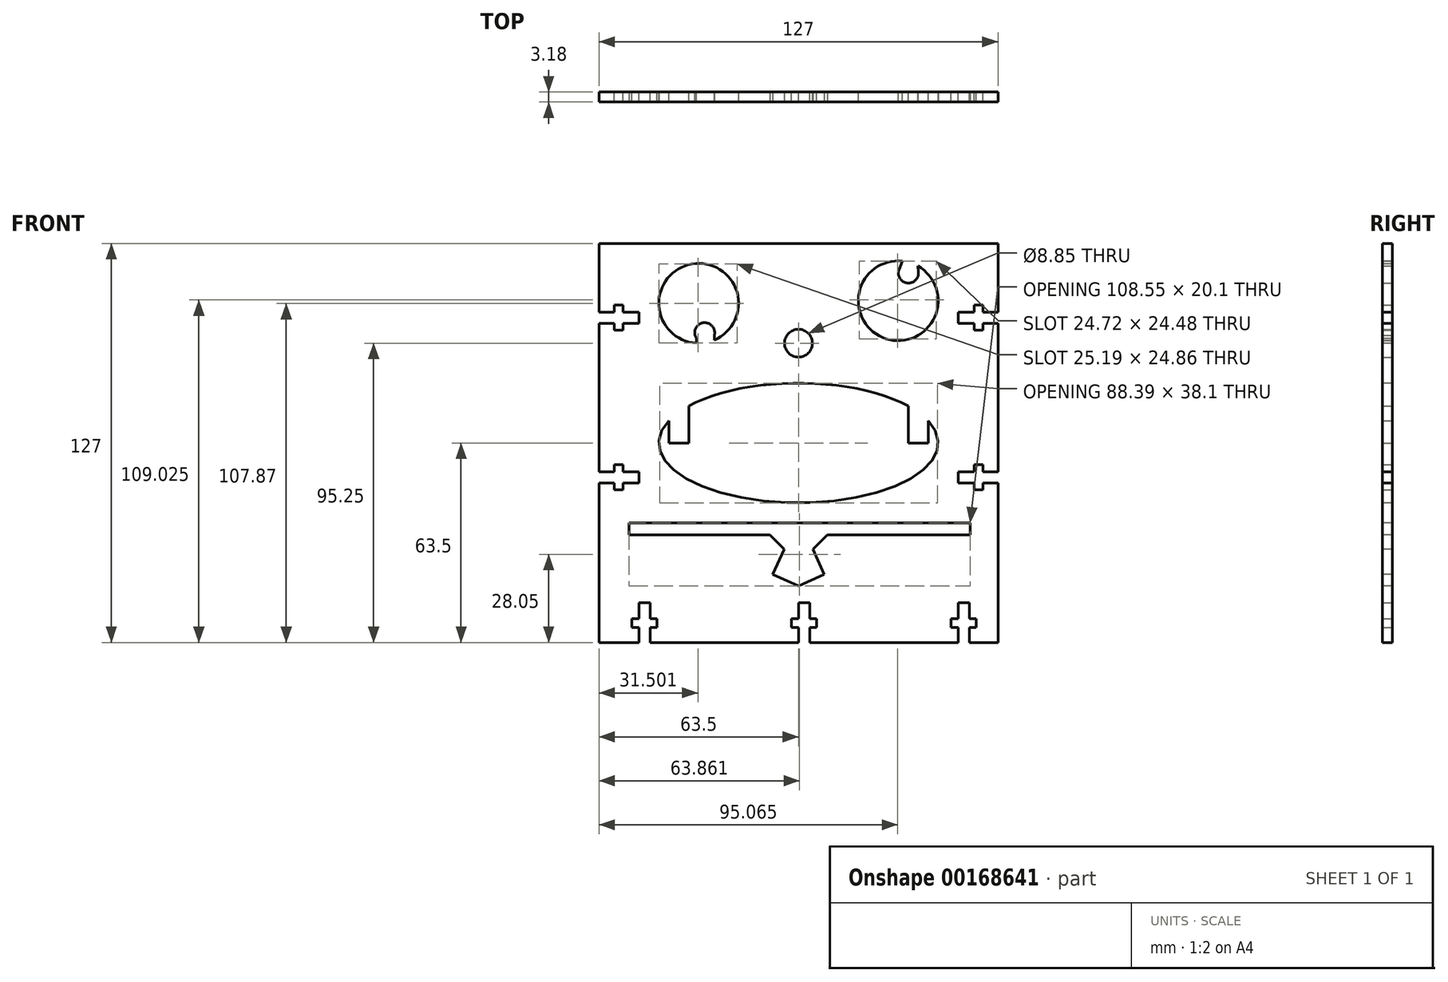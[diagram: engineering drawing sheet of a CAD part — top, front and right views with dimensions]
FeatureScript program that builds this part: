
annotation { "Feature Type Name" : "Feature", "Feature Type Description" : "" }
export const myFeature = defineFeature(function(context is Context, id is Id, definition is map)
    precondition{}
    {
        {
            var Q0;
            Q0=qCreatedBy(makeId("Front.planeOp"),FACE);
            var sketch = newSketch(context, id + "F0", { "sketchPlane" : qUnion([Q0])});
            skLineSegment(sketch, "E0.bottom", {"start": v(63.5, -63.5) * mm, "end": v(-63.5, -63.5) * mm});
            skLineSegment(sketch, "E0.top", {"start": v(63.5, 63.5) * mm, "end": v(-63.5, 63.5) * mm});
            skLineSegment(sketch, "E0.left", {"start": v(63.5, -63.5) * mm, "end": v(63.5, 63.5) * mm});
            skLineSegment(sketch, "E0.right", {"start": v(-63.5, -63.5) * mm, "end": v(-63.5, 63.5) * mm});
            skPoint(sketch, "E0.middle", {"position": v(0, 0) * mm});
            skEllipse(sketch, "E1", {"center": v(0, 0) * mm, "majorRadius": 44.45 * mm, "minorRadius": 19.05 * mm, "majorAxis": v(1, 0)});
            skLineSegment(sketch, "E2", {"start": v(-34.93, 11.78) * mm, "end": v(-34.93, 0) * mm});
            skLineSegment(sketch, "E3", {"start": v(-41.28, 0) * mm, "end": v(-34.93, 0) * mm});
            skLineSegment(sketch, "E4", {"start": v(-41.28, 0) * mm, "end": v(-41.28, 7.07) * mm});
            skLineSegment(sketch, "E5", {"start": v(41.28, 7.07) * mm, "end": v(41.28, 0) * mm});
            skLineSegment(sketch, "E6", {"start": v(34.93, 0) * mm, "end": v(41.28, 0) * mm});
            skLineSegment(sketch, "E7", {"start": v(34.93, 0) * mm, "end": v(34.93, 11.78) * mm});
            skCircle(sketch, "E8", {"center": v(0, 31.75) * mm, "radius": 4.43 * mm});
            skCircle(sketch, "E9", {"center": v(-31.75, 44.45) * mm, "radius": 12.7 * mm});
            skArc(sketch, "E10", {"start": v(-26.78, 34.27) * mm, "mid": v(-30.31, 38.26) * mm, "end": v(-32.52, 33.41) * mm});
            skCircle(sketch, "E11", {"center": v(31.75, 45.26) * mm, "radius": 12.7 * mm});
            skArc(sketch, "E12", {"start": v(32.04, 55.22) * mm, "mid": v(34.52, 50.92) * mm, "end": v(38.17, 54.28) * mm});
            skLineSegment(sketch, "E13", {"start": v(32.04, 55.22) * mm, "end": v(33.09, 57.88) * mm});
            skLineSegment(sketch, "E14", {"start": v(38.17, 54.28) * mm, "end": v(38.03, 56.3) * mm});
            skLineSegment(sketch, "E15", {"start": v(-32.52, 33.41) * mm, "end": v(-32.52, 31.77) * mm});
            skLineSegment(sketch, "E16", {"start": v(-26.78, 34.27) * mm, "end": v(-26.78, 32.76) * mm});
            skLineSegment(sketch, "E17", {"start": v(-50.8, -58.66) * mm, "end": v(-50.8, -63.5) * mm});
            skLineSegment(sketch, "E18", {"start": v(-50.8, -58.66) * mm, "end": v(-53, -58.66) * mm});
            skLineSegment(sketch, "E19", {"start": v(-53, -58.66) * mm, "end": v(-53, -55.88) * mm});
            skLineSegment(sketch, "E20", {"start": v(-53, -55.88) * mm, "end": v(-50.8, -55.88) * mm});
            skLineSegment(sketch, "E21", {"start": v(-50.8, -55.88) * mm, "end": v(-50.8, -50.8) * mm});
            skLineSegment(sketch, "E22", {"start": v(-50.8, -50.8) * mm, "end": v(-47.24, -50.8) * mm});
            skLineSegment(sketch, "E23", {"start": v(-47.24, -50.8) * mm, "end": v(-47.24, -55.88) * mm});
            skLineSegment(sketch, "E24", {"start": v(-47.24, -55.88) * mm, "end": v(-45.05, -55.88) * mm});
            skLineSegment(sketch, "E25", {"start": v(-45.05, -55.88) * mm, "end": v(-45.05, -58.66) * mm});
            skLineSegment(sketch, "E26", {"start": v(-45.05, -58.66) * mm, "end": v(-47.24, -58.66) * mm});
            skLineSegment(sketch, "E27", {"start": v(-47.24, -58.66) * mm, "end": v(-47.24, -63.5) * mm});
            skLineSegment(sketch, "E28.1.0.0", {"start": v(0, -58.66) * mm, "end": v(0, -63.5) * mm});
            skLineSegment(sketch, "E28.1.0.1", {"start": v(3.56, -58.66) * mm, "end": v(3.56, -63.5) * mm});
            skLineSegment(sketch, "E28.1.0.2", {"start": v(3.56, -50.8) * mm, "end": v(3.56, -55.88) * mm});
            skLineSegment(sketch, "E28.1.0.3", {"start": v(-2.2, -55.88) * mm, "end": v(0, -55.88) * mm});
            skLineSegment(sketch, "E28.1.0.4", {"start": v(0, -55.88) * mm, "end": v(0, -50.8) * mm});
            skLineSegment(sketch, "E28.1.0.5", {"start": v(0, -58.66) * mm, "end": v(-2.2, -58.66) * mm});
            skLineSegment(sketch, "E28.1.0.6", {"start": v(0, -50.8) * mm, "end": v(3.56, -50.8) * mm});
            skLineSegment(sketch, "E28.1.0.7", {"start": v(-2.2, -58.66) * mm, "end": v(-2.2, -55.88) * mm});
            skLineSegment(sketch, "E28.1.0.8", {"start": v(3.56, -55.88) * mm, "end": v(5.75, -55.88) * mm});
            skLineSegment(sketch, "E28.1.0.9", {"start": v(5.75, -55.88) * mm, "end": v(5.75, -58.66) * mm});
            skLineSegment(sketch, "E28.1.0.10", {"start": v(5.75, -58.66) * mm, "end": v(3.56, -58.66) * mm});
            skLineSegment(sketch, "E28.2.0.0", {"start": v(50.8, -58.66) * mm, "end": v(50.8, -63.5) * mm});
            skLineSegment(sketch, "E28.2.0.1", {"start": v(54.36, -58.66) * mm, "end": v(54.36, -63.5) * mm});
            skLineSegment(sketch, "E28.2.0.2", {"start": v(54.36, -50.8) * mm, "end": v(54.36, -55.88) * mm});
            skLineSegment(sketch, "E28.2.0.3", {"start": v(48.6, -55.88) * mm, "end": v(50.8, -55.88) * mm});
            skLineSegment(sketch, "E28.2.0.4", {"start": v(50.8, -55.88) * mm, "end": v(50.8, -50.8) * mm});
            skLineSegment(sketch, "E28.2.0.5", {"start": v(50.8, -58.66) * mm, "end": v(48.6, -58.66) * mm});
            skLineSegment(sketch, "E28.2.0.6", {"start": v(50.8, -50.8) * mm, "end": v(54.36, -50.8) * mm});
            skLineSegment(sketch, "E28.2.0.7", {"start": v(48.6, -58.66) * mm, "end": v(48.6, -55.88) * mm});
            skLineSegment(sketch, "E28.2.0.8", {"start": v(54.36, -55.88) * mm, "end": v(56.55, -55.88) * mm});
            skLineSegment(sketch, "E28.2.0.9", {"start": v(56.55, -55.88) * mm, "end": v(56.55, -58.66) * mm});
            skLineSegment(sketch, "E28.2.0.10", {"start": v(56.55, -58.66) * mm, "end": v(54.36, -58.66) * mm});
            skLineSegment(sketch, "E28.direction1", {"start": v(-50.8, -63.5) * mm, "end": v(0, -63.5) * mm, "construction": true});
            skLineSegment(sketch, "E29", {"start": v(-63.5, -12.7) * mm, "end": v(-58.66, -12.7) * mm});
            skLineSegment(sketch, "E30", {"start": v(-58.66, -12.7) * mm, "end": v(-58.66, -14.9) * mm});
            skLineSegment(sketch, "E31", {"start": v(-58.66, -14.9) * mm, "end": v(-55.88, -14.9) * mm});
            skLineSegment(sketch, "E32", {"start": v(-55.88, -14.9) * mm, "end": v(-55.88, -12.7) * mm});
            skLineSegment(sketch, "E33", {"start": v(-55.88, -12.7) * mm, "end": v(-50.8, -12.7) * mm});
            skLineSegment(sketch, "E34", {"start": v(-50.8, -12.7) * mm, "end": v(-50.8, -9.14) * mm});
            skLineSegment(sketch, "E35", {"start": v(-50.8, -9.14) * mm, "end": v(-55.88, -9.14) * mm});
            skLineSegment(sketch, "E36", {"start": v(-55.88, -9.14) * mm, "end": v(-55.88, -6.95) * mm});
            skLineSegment(sketch, "E37", {"start": v(-55.88, -6.95) * mm, "end": v(-58.66, -6.95) * mm});
            skLineSegment(sketch, "E38", {"start": v(-58.66, -6.95) * mm, "end": v(-58.66, -9.14) * mm});
            skLineSegment(sketch, "E39", {"start": v(-58.66, -9.14) * mm, "end": v(-63.5, -9.14) * mm});
            skLineSegment(sketch, "E40.0.1.0", {"start": v(-58.66, 41.66) * mm, "end": v(-63.5, 41.66) * mm});
            skLineSegment(sketch, "E40.0.1.1", {"start": v(-50.8, 41.66) * mm, "end": v(-55.88, 41.66) * mm});
            skLineSegment(sketch, "E40.0.1.2", {"start": v(-50.8, 38.1) * mm, "end": v(-50.8, 41.66) * mm});
            skLineSegment(sketch, "E40.0.1.3", {"start": v(-63.5, 38.1) * mm, "end": v(-58.66, 38.1) * mm});
            skLineSegment(sketch, "E40.0.1.4", {"start": v(-55.88, 38.1) * mm, "end": v(-50.8, 38.1) * mm});
            skLineSegment(sketch, "E40.0.1.5", {"start": v(-55.88, 43.85) * mm, "end": v(-58.66, 43.85) * mm});
            skLineSegment(sketch, "E40.0.1.6", {"start": v(-55.88, 41.66) * mm, "end": v(-55.88, 43.85) * mm});
            skLineSegment(sketch, "E40.0.1.7", {"start": v(-58.66, 38.1) * mm, "end": v(-58.66, 35.9) * mm});
            skLineSegment(sketch, "E40.0.1.8", {"start": v(-58.66, 35.9) * mm, "end": v(-55.88, 35.9) * mm});
            skLineSegment(sketch, "E40.0.1.9", {"start": v(-55.88, 35.9) * mm, "end": v(-55.88, 38.1) * mm});
            skLineSegment(sketch, "E40.0.1.10", {"start": v(-58.66, 43.85) * mm, "end": v(-58.66, 41.66) * mm});
            skLineSegment(sketch, "E40.direction1", {"start": v(-63.5, -12.7) * mm, "end": v(-38.1, -12.7) * mm, "construction": true});
            skLineSegment(sketch, "E40.direction2", {"start": v(-63.5, -12.7) * mm, "end": v(-63.5, 38.1) * mm, "construction": true});
            skLineSegment(sketch, "E41.MirrorCS", {"start": v(55.88, -14.9) * mm, "end": v(55.88, -12.7) * mm});
            skLineSegment(sketch, "E42.MirrorCS", {"start": v(58.66, -14.9) * mm, "end": v(55.88, -14.9) * mm});
            skLineSegment(sketch, "E43.MirrorCS", {"start": v(58.66, -12.7) * mm, "end": v(58.66, -14.9) * mm});
            skLineSegment(sketch, "E44.MirrorCS", {"start": v(63.5, -12.7) * mm, "end": v(58.66, -12.7) * mm});
            skLineSegment(sketch, "E45.MirrorCS", {"start": v(58.66, 35.9) * mm, "end": v(55.88, 35.9) * mm});
            skLineSegment(sketch, "E46.MirrorCS", {"start": v(58.66, 38.1) * mm, "end": v(58.66, 35.9) * mm});
            skLineSegment(sketch, "E47.MirrorCS", {"start": v(58.66, -6.95) * mm, "end": v(58.66, -9.14) * mm});
            skLineSegment(sketch, "E48.MirrorCS", {"start": v(55.88, 43.85) * mm, "end": v(58.66, 43.85) * mm});
            skLineSegment(sketch, "E49.MirrorCS", {"start": v(55.88, 35.9) * mm, "end": v(55.88, 38.1) * mm});
            skLineSegment(sketch, "E50.MirrorCS", {"start": v(58.66, -9.14) * mm, "end": v(63.5, -9.14) * mm});
            skLineSegment(sketch, "E51.MirrorCS", {"start": v(55.88, -6.95) * mm, "end": v(58.66, -6.95) * mm});
            skLineSegment(sketch, "E52.MirrorCS", {"start": v(50.8, -12.7) * mm, "end": v(50.8, -9.14) * mm});
            skLineSegment(sketch, "E53.MirrorCS", {"start": v(55.88, -9.14) * mm, "end": v(55.88, -6.95) * mm});
            skLineSegment(sketch, "E54.MirrorCS", {"start": v(55.88, -12.7) * mm, "end": v(50.8, -12.7) * mm});
            skLineSegment(sketch, "E55.MirrorCS", {"start": v(55.88, 41.66) * mm, "end": v(55.88, 43.85) * mm});
            skLineSegment(sketch, "E56.MirrorCS", {"start": v(58.66, 43.85) * mm, "end": v(58.66, 41.66) * mm});
            skLineSegment(sketch, "E57.MirrorCS", {"start": v(50.8, 41.66) * mm, "end": v(55.88, 41.66) * mm});
            skLineSegment(sketch, "E58.MirrorCS", {"start": v(58.66, 41.66) * mm, "end": v(63.5, 41.66) * mm});
            skLineSegment(sketch, "E59.MirrorCS", {"start": v(50.8, 38.1) * mm, "end": v(50.8, 41.66) * mm});
            skLineSegment(sketch, "E60.MirrorCS", {"start": v(55.88, 38.1) * mm, "end": v(50.8, 38.1) * mm});
            skLineSegment(sketch, "E61.MirrorCS", {"start": v(63.5, 38.1) * mm, "end": v(58.66, 38.1) * mm});
            skLineSegment(sketch, "E62.MirrorCS", {"start": v(50.8, -9.14) * mm, "end": v(55.88, -9.14) * mm});
            skLineSegment(sketch, "E63.MirrorCS", {"start": v(63.5, -12.7) * mm, "end": v(63.5, 38.1) * mm, "construction": true});
            skSolve(sketch);
        }
        {
            var Q0;
            {var subQ27=sQuery(id+"F0.wireOp",EDGE,"E0.top");Q0=makeQuery(id+"F0.imprint","IMPRINT",FACE,{"disambiguationData":[TD([[makeQuery(id+"F0.imprint","IMPRINT",EDGE,{"derivedFrom":subQ27}),1.0]])]});}
            var Q1;
            Q1=makeQuery(id+"F0.imprint","IMPRINT",FACE,{"disambiguationData":[TD([[makeQuery(id+"F0.imprint","IMPRINT",EDGE,{"derivedFrom":sQuery(id+"F0.wireOp",EDGE,"E12")}),1.0]])]});
            var Q2;
            Q2=makeQuery(id+"F0.imprint","IMPRINT",FACE,{"disambiguationData":[TD([[makeQuery(id+"F0.imprint","IMPRINT",EDGE,{"derivedFrom":sQuery(id+"F0.wireOp",EDGE,"E10")}),1.0]])]});
            var Q3;
            {var subQ0=sQuery(id+"F0.wireOp",EDGE,"E2");Q3=makeQuery(id+"F0.imprint","IMPRINT",FACE,{"disambiguationData":[TD([[makeQuery(id+"F0.imprint","IMPRINT",EDGE,{"derivedFrom":subQ0}),-1.0]])]});}
            var Q4;
            {var subQ0=sQuery(id+"F0.wireOp",EDGE,"E5");Q4=makeQuery(id+"F0.imprint","IMPRINT",FACE,{"disambiguationData":[TD([[makeQuery(id+"F0.imprint","IMPRINT",EDGE,{"derivedFrom":subQ0}),-1.0]])]});}
            extrude(context, id + "F1", {"entities" : qUnion([Q0, Q1, Q2, Q3, Q4]), "endBound" : BoundingType.SYMMETRIC, "depth" : 3.17 * mm});
        }
        {
            var Q0;
            Q0=makeQuery(id+"F1.opExtrude","CAP_FACE",FACE,{"disambiguationData":[OSD([sQuery(id+"F0.wireOp",EDGE,"E0.bottom"),sQuery(id+"F0.wireOp",EDGE,"E0.top"),sQuery(id+"F0.wireOp",EDGE,"E0.left"),sQuery(id+"F0.wireOp",EDGE,"E0.right"),sQuery(id+"F0.wireOp",EDGE,"E1"),sQuery(id+"F0.wireOp",EDGE,"E2"),sQuery(id+"F0.wireOp",EDGE,"E3"),sQuery(id+"F0.wireOp",EDGE,"E4"),sQuery(id+"F0.wireOp",EDGE,"E5"),sQuery(id+"F0.wireOp",EDGE,"E6"),sQuery(id+"F0.wireOp",EDGE,"E7"),sQuery(id+"F0.wireOp",EDGE,"E8"),sQuery(id+"F0.wireOp",EDGE,"E9"),sQuery(id+"F0.wireOp",EDGE,"E10"),sQuery(id+"F0.wireOp",EDGE,"E11"),sQuery(id+"F0.wireOp",EDGE,"E12"),sQuery(id+"F0.wireOp",EDGE,"E13"),sQuery(id+"F0.wireOp",EDGE,"E14"),sQuery(id+"F0.wireOp",EDGE,"E15"),sQuery(id+"F0.wireOp",EDGE,"E16"),sQuery(id+"F0.wireOp",EDGE,"E17"),sQuery(id+"F0.wireOp",EDGE,"E18"),sQuery(id+"F0.wireOp",EDGE,"E19"),sQuery(id+"F0.wireOp",EDGE,"E20"),sQuery(id+"F0.wireOp",EDGE,"E21"),sQuery(id+"F0.wireOp",EDGE,"E22"),sQuery(id+"F0.wireOp",EDGE,"E23"),sQuery(id+"F0.wireOp",EDGE,"E24"),sQuery(id+"F0.wireOp",EDGE,"E25"),sQuery(id+"F0.wireOp",EDGE,"E26"),sQuery(id+"F0.wireOp",EDGE,"E27"),sQuery(id+"F0.wireOp",EDGE,"E28.1.0.0"),sQuery(id+"F0.wireOp",EDGE,"E28.1.0.1"),sQuery(id+"F0.wireOp",EDGE,"E28.1.0.2"),sQuery(id+"F0.wireOp",EDGE,"E28.1.0.3"),sQuery(id+"F0.wireOp",EDGE,"E28.1.0.4"),sQuery(id+"F0.wireOp",EDGE,"E28.1.0.5"),sQuery(id+"F0.wireOp",EDGE,"E28.1.0.6"),sQuery(id+"F0.wireOp",EDGE,"E28.1.0.7"),sQuery(id+"F0.wireOp",EDGE,"E28.1.0.8"),sQuery(id+"F0.wireOp",EDGE,"E28.1.0.9"),sQuery(id+"F0.wireOp",EDGE,"E28.1.0.10"),sQuery(id+"F0.wireOp",EDGE,"E28.2.0.0"),sQuery(id+"F0.wireOp",EDGE,"E28.2.0.1"),sQuery(id+"F0.wireOp",EDGE,"E28.2.0.2"),sQuery(id+"F0.wireOp",EDGE,"E28.2.0.3"),sQuery(id+"F0.wireOp",EDGE,"E28.2.0.4"),sQuery(id+"F0.wireOp",EDGE,"E28.2.0.5"),sQuery(id+"F0.wireOp",EDGE,"E28.2.0.6"),sQuery(id+"F0.wireOp",EDGE,"E28.2.0.7"),sQuery(id+"F0.wireOp",EDGE,"E28.2.0.8"),sQuery(id+"F0.wireOp",EDGE,"E28.2.0.9"),sQuery(id+"F0.wireOp",EDGE,"E28.2.0.10"),sQuery(id+"F0.wireOp",EDGE,"E29"),sQuery(id+"F0.wireOp",EDGE,"E30"),sQuery(id+"F0.wireOp",EDGE,"E31"),sQuery(id+"F0.wireOp",EDGE,"E32"),sQuery(id+"F0.wireOp",EDGE,"E33"),sQuery(id+"F0.wireOp",EDGE,"E34"),sQuery(id+"F0.wireOp",EDGE,"E35"),sQuery(id+"F0.wireOp",EDGE,"E36"),sQuery(id+"F0.wireOp",EDGE,"E37"),sQuery(id+"F0.wireOp",EDGE,"E38"),sQuery(id+"F0.wireOp",EDGE,"E39"),sQuery(id+"F0.wireOp",EDGE,"E40.0.1.0"),sQuery(id+"F0.wireOp",EDGE,"E40.0.1.1"),sQuery(id+"F0.wireOp",EDGE,"E40.0.1.2"),sQuery(id+"F0.wireOp",EDGE,"E40.0.1.3"),sQuery(id+"F0.wireOp",EDGE,"E40.0.1.4"),sQuery(id+"F0.wireOp",EDGE,"E40.0.1.5"),sQuery(id+"F0.wireOp",EDGE,"E40.0.1.6"),sQuery(id+"F0.wireOp",EDGE,"E40.0.1.7"),sQuery(id+"F0.wireOp",EDGE,"E40.0.1.8"),sQuery(id+"F0.wireOp",EDGE,"E40.0.1.9"),sQuery(id+"F0.wireOp",EDGE,"E40.0.1.10"),sQuery(id+"F0.wireOp",EDGE,"E41.MirrorCS"),sQuery(id+"F0.wireOp",EDGE,"E42.MirrorCS"),sQuery(id+"F0.wireOp",EDGE,"E43.MirrorCS"),sQuery(id+"F0.wireOp",EDGE,"E44.MirrorCS"),sQuery(id+"F0.wireOp",EDGE,"E45.MirrorCS"),sQuery(id+"F0.wireOp",EDGE,"E46.MirrorCS"),sQuery(id+"F0.wireOp",EDGE,"E47.MirrorCS"),sQuery(id+"F0.wireOp",EDGE,"E48.MirrorCS"),sQuery(id+"F0.wireOp",EDGE,"E49.MirrorCS"),sQuery(id+"F0.wireOp",EDGE,"E50.MirrorCS"),sQuery(id+"F0.wireOp",EDGE,"E51.MirrorCS"),sQuery(id+"F0.wireOp",EDGE,"E52.MirrorCS"),sQuery(id+"F0.wireOp",EDGE,"E53.MirrorCS"),sQuery(id+"F0.wireOp",EDGE,"E54.MirrorCS"),sQuery(id+"F0.wireOp",EDGE,"E55.MirrorCS"),sQuery(id+"F0.wireOp",EDGE,"E56.MirrorCS"),sQuery(id+"F0.wireOp",EDGE,"E57.MirrorCS"),sQuery(id+"F0.wireOp",EDGE,"E58.MirrorCS"),sQuery(id+"F0.wireOp",EDGE,"E59.MirrorCS"),sQuery(id+"F0.wireOp",EDGE,"E60.MirrorCS"),sQuery(id+"F0.wireOp",EDGE,"E61.MirrorCS"),sQuery(id+"F0.wireOp",EDGE,"E62.MirrorCS")])],"isStart":false});
            var sketch = newSketch(context, id + "F2", { "sketchPlane" : qUnion([Q0])});
            skLineSegment(sketch, "E64", {"start": v(-53.92, -29.21) * mm, "end": v(54.64, -29.21) * mm});
            skLineSegment(sketch, "E65", {"start": v(-9.15, -29.21) * mm, "end": v(0, -38.36) * mm});
            skLineSegment(sketch, "E66", {"start": v(0, -38.36) * mm, "end": v(9.15, -29.21) * mm});
            skLineSegment(sketch, "E67", {"start": v(-4.58, -33.79) * mm, "end": v(-8.2, -41.78) * mm});
            skLineSegment(sketch, "E68", {"start": v(-8.2, -41.78) * mm, "end": v(0, -45.5) * mm});
            skLineSegment(sketch, "E69", {"start": v(0, -45.5) * mm, "end": v(8.2, -41.78) * mm});
            skLineSegment(sketch, "E70", {"start": v(8.2, -41.78) * mm, "end": v(4.58, -33.79) * mm});
            skLineSegment(sketch, "E71", {"start": v(54.64, -29.21) * mm, "end": v(54.64, -25.4) * mm});
            skLineSegment(sketch, "E72", {"start": v(54.64, -25.4) * mm, "end": v(-53.92, -25.4) * mm});
            skLineSegment(sketch, "E73", {"start": v(-53.92, -25.4) * mm, "end": v(-53.92, -29.21) * mm});
            skSolve(sketch);
        }
        {
            var Q0;
            Q0 = qSketchRegion(id + "F2", true);
            var Q1;
            Q1=sQuery(id+"F2.wireOp",EDGE,"E65");
            var Q2;
            Q2=sQuery(id+"F2.wireOp",EDGE,"E64");
            var Q3;
            Q3=sQuery(id+"F2.wireOp",EDGE,"E66");
            var Q4;
            Q4=sQuery(id+"F2.wireOp",EDGE,"E69");
            var Q5;
            Q5=sQuery(id+"F2.wireOp",EDGE,"E70");
            var Q6;
            Q6=sQuery(id+"F2.wireOp",EDGE,"E68");
            var Q7;
            Q7=sQuery(id+"F2.wireOp",EDGE,"E67");
            extrude(context, id + "F3", {"entities" : qUnion([Q0]), "operationType" : NewBodyOperationType.REMOVE, "surfaceEntities" : qUnion([Q1, Q2, Q3, Q4, Q5, Q6, Q7]), "endBound" : BoundingType.THROUGH_ALL, "oppositeDirection" : true, "depth" : 25.4 * mm});
        }
    });
